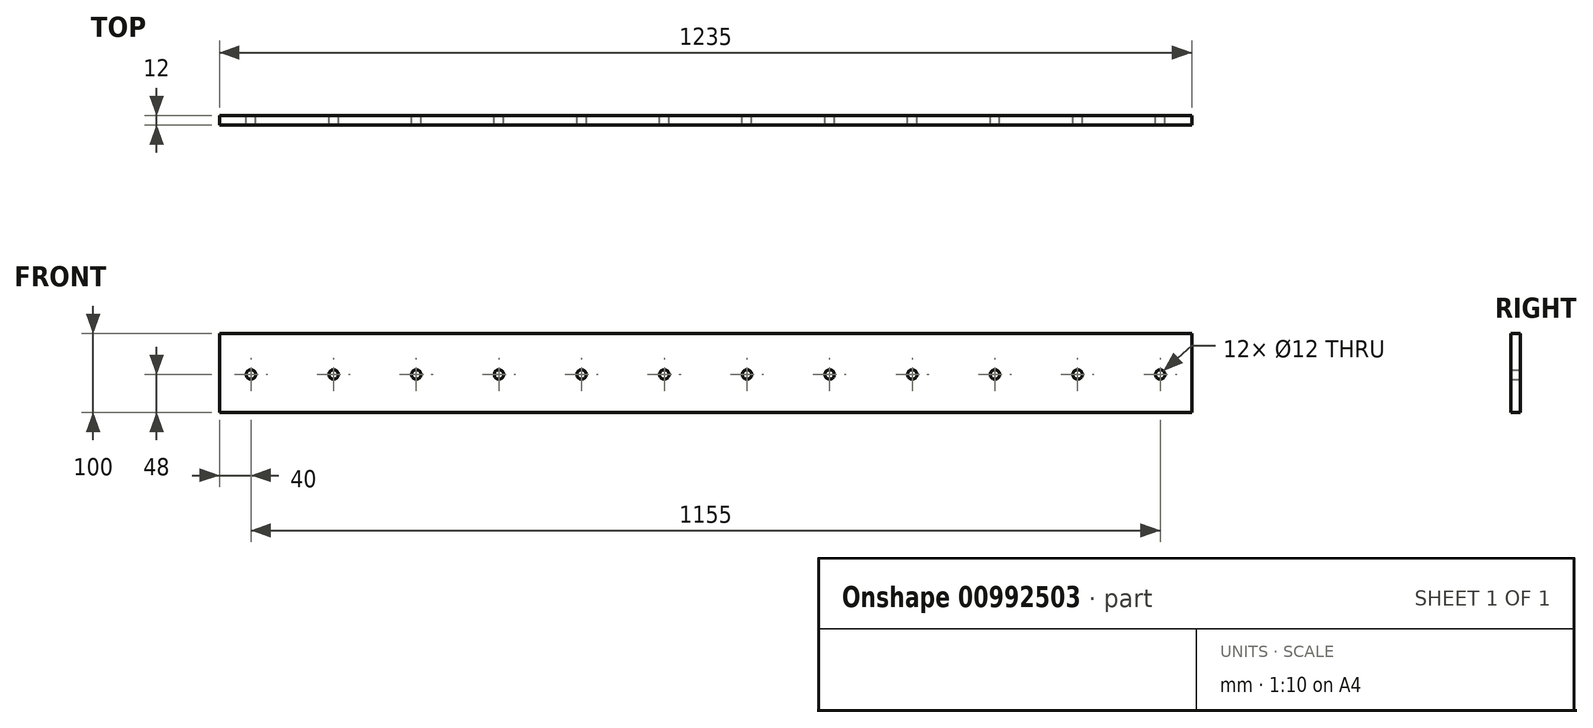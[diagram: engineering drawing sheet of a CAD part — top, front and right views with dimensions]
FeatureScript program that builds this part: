
annotation { "Feature Type Name" : "Feature", "Feature Type Description" : "" }
export const myFeature = defineFeature(function(context is Context, id is Id, definition is map)
    precondition{}
    {
        {
            var Q0;
            Q0=qCreatedBy(makeId("Front.planeOp"),FACE);
            var sketch = newSketch(context, id + "F0", { "sketchPlane" : qUnion([Q0])});
            skLineSegment(sketch, "E0.bottom", {"start": v(-617.5, 100) * mm, "end": v(617.5, 100) * mm});
            skLineSegment(sketch, "E0.top", {"start": v(-617.5, 0) * mm, "end": v(617.5, 0) * mm});
            skLineSegment(sketch, "E0.left", {"start": v(-617.5, 100) * mm, "end": v(-617.5, 0) * mm});
            skLineSegment(sketch, "E0.right", {"start": v(617.5, 100) * mm, "end": v(617.5, 0) * mm});
            skCircle(sketch, "E1", {"center": v(-577.5, 48) * mm, "radius": 6 * mm});
            skCircle(sketch, "E2.1.0.0", {"center": v(-472.5, 48) * mm, "radius": 6 * mm});
            skCircle(sketch, "E2.2.0.0", {"center": v(-367.5, 48) * mm, "radius": 6 * mm});
            skCircle(sketch, "E2.3.0.0", {"center": v(-262.5, 48) * mm, "radius": 6 * mm});
            skCircle(sketch, "E2.4.0.0", {"center": v(-157.5, 48) * mm, "radius": 6 * mm});
            skCircle(sketch, "E2.5.0.0", {"center": v(-52.5, 48) * mm, "radius": 6 * mm});
            skCircle(sketch, "E2.6.0.0", {"center": v(52.5, 48) * mm, "radius": 6 * mm});
            skCircle(sketch, "E2.7.0.0", {"center": v(157.5, 48) * mm, "radius": 6 * mm});
            skCircle(sketch, "E2.8.0.0", {"center": v(262.5, 48) * mm, "radius": 6 * mm});
            skCircle(sketch, "E2.9.0.0", {"center": v(367.5, 48) * mm, "radius": 6 * mm});
            skCircle(sketch, "E2.10.0.0", {"center": v(472.5, 48) * mm, "radius": 6 * mm});
            skCircle(sketch, "E2.11.0.0", {"center": v(577.5, 48) * mm, "radius": 6 * mm});
            skLineSegment(sketch, "E2.direction1", {"start": v(-577.5, 48) * mm, "end": v(-472.5, 48) * mm, "construction": true});
            skSolve(sketch);
        }
        {
            var Q0;
            Q0 = qSketchRegion(id + "F0", true);
            extrude(context, id + "F1", {"entities" : qUnion([Q0]), "depth" : 12 * mm, "offsetDistance" : 25 * mm});
        }
    });
